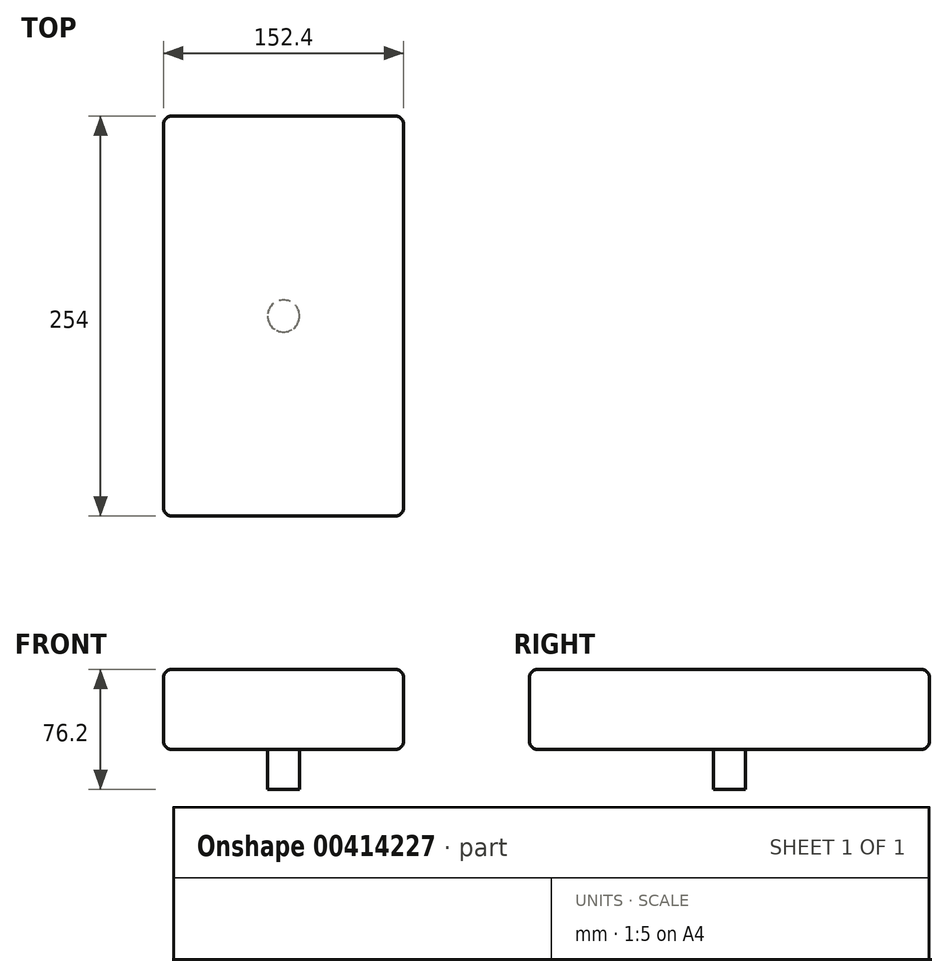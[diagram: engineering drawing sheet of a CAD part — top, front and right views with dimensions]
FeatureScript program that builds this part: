
annotation { "Feature Type Name" : "Feature", "Feature Type Description" : "" }
export const myFeature = defineFeature(function(context is Context, id is Id, definition is map)
    precondition{}
    {
        {
            var Q0;
            Q0=qCreatedBy(makeId("Top.planeOp"),FACE);
            var sketch = newSketch(context, id + "F0", { "sketchPlane" : qUnion([Q0])});
            skLineSegment(sketch, "E0.bottom", {"start": v(76.2, 127) * mm, "end": v(-76.2, 127) * mm});
            skLineSegment(sketch, "E0.top", {"start": v(76.2, -127) * mm, "end": v(-76.2, -127) * mm});
            skLineSegment(sketch, "E0.left", {"start": v(76.2, 127) * mm, "end": v(76.2, -127) * mm});
            skLineSegment(sketch, "E0.right", {"start": v(-76.2, 127) * mm, "end": v(-76.2, -127) * mm});
            skPoint(sketch, "E0.middle", {"position": v(0, 0) * mm});
            skSolve(sketch);
        }
        {
            var Q0;
            Q0=makeQuery(id+"F0.imprint","IMPRINT",FACE,{"disambiguationData":[TD([[makeQuery(id+"F0.imprint","IMPRINT",EDGE,{"derivedFrom":sQuery(id+"F0.wireOp",EDGE,"E0.bottom")}),1.0]])]});
            extrude(context, id + "F1", {"entities" : qUnion([Q0]), "depth" : 50.8 * mm});
        }
        {
            var Q0;
            Q0=makeQuery(id+"F1.opExtrude","CAP_EDGE",EDGE,{"disambiguationData":[OSD([sQuery(id+"F0.wireOp",EDGE,"E0.right")])],"isStart":false});
            var Q1;
            Q1=makeQuery(id+"F1.opExtrude","SWEPT_EDGE",EDGE,{"disambiguationData":[OSD([sQuery(id+"F0.wireOp",EDGE,"E0.bottom"),sQuery(id+"F0.wireOp",EDGE,"E0.right")])]});
            var Q2;
            Q2=makeQuery(id+"F1.opExtrude","CAP_EDGE",EDGE,{"disambiguationData":[OSD([sQuery(id+"F0.wireOp",EDGE,"E0.right")])],"isStart":true});
            var Q3;
            Q3=makeQuery(id+"F1.opExtrude","SWEPT_EDGE",EDGE,{"disambiguationData":[OSD([sQuery(id+"F0.wireOp",EDGE,"E0.top"),sQuery(id+"F0.wireOp",EDGE,"E0.right")])]});
            var Q4;
            Q4=makeQuery(id+"F1.opExtrude","CAP_EDGE",EDGE,{"disambiguationData":[OSD([sQuery(id+"F0.wireOp",EDGE,"E0.top")])],"isStart":false});
            var Q5;
            Q5=makeQuery(id+"F1.opExtrude","CAP_EDGE",EDGE,{"disambiguationData":[OSD([sQuery(id+"F0.wireOp",EDGE,"E0.top")])],"isStart":true});
            var Q6;
            Q6=makeQuery(id+"F1.opExtrude","SWEPT_EDGE",EDGE,{"disambiguationData":[OSD([sQuery(id+"F0.wireOp",EDGE,"E0.top"),sQuery(id+"F0.wireOp",EDGE,"E0.left")])]});
            var Q7;
            Q7=makeQuery(id+"F1.opExtrude","CAP_EDGE",EDGE,{"disambiguationData":[OSD([sQuery(id+"F0.wireOp",EDGE,"E0.left")])],"isStart":false});
            var Q8;
            Q8=makeQuery(id+"F1.opExtrude","CAP_EDGE",EDGE,{"disambiguationData":[OSD([sQuery(id+"F0.wireOp",EDGE,"E0.left")])],"isStart":true});
            var Q9;
            Q9=makeQuery(id+"F1.opExtrude","SWEPT_EDGE",EDGE,{"disambiguationData":[OSD([sQuery(id+"F0.wireOp",EDGE,"E0.bottom"),sQuery(id+"F0.wireOp",EDGE,"E0.left")])]});
            var Q10;
            Q10=makeQuery(id+"F1.opExtrude","CAP_EDGE",EDGE,{"disambiguationData":[OSD([sQuery(id+"F0.wireOp",EDGE,"E0.bottom")])],"isStart":true});
            var Q11;
            Q11=makeQuery(id+"F1.opExtrude","SWEPT_FACE",FACE,{"disambiguationData":[OSD([sQuery(id+"F0.wireOp",EDGE,"E0.bottom")])]});
            fillet(context, id + "F2", {"entities" : qUnion([Q0, Q1, Q2, Q3, Q4, Q5, Q6, Q7, Q8, Q9, Q10, Q11]), "radius" : 5.08 * mm, "tangentPropagation" : true, "allowEdgeOverflow" : false});
        }
        {
            var Q0;
            Q0=makeQuery(id+"F1.opExtrude","CAP_FACE",FACE,{"disambiguationData":[OSD([sQuery(id+"F0.wireOp",EDGE,"E0.bottom"),sQuery(id+"F0.wireOp",EDGE,"E0.top"),sQuery(id+"F0.wireOp",EDGE,"E0.left"),sQuery(id+"F0.wireOp",EDGE,"E0.right")])],"isStart":true});
            var sketch = newSketch(context, id + "F3", { "sketchPlane" : qUnion([Q0])});
            skCircle(sketch, "E1", {"center": v(0, 0) * mm, "radius": 10.16 * mm});
            skSolve(sketch);
        }
        {
            var Q0;
            Q0=makeQuery(id+"F3.imprint","IMPRINT",FACE,{"disambiguationData":[TD([[makeQuery(id+"F3.imprint","IMPRINT",EDGE,{"derivedFrom":sQuery(id+"F3.wireOp",EDGE,"E1")}),1.0]])]});
            extrude(context, id + "F4", {"entities" : qUnion([Q0]), "operationType" : NewBodyOperationType.ADD, "depth" : 25.4 * mm});
        }
    });
